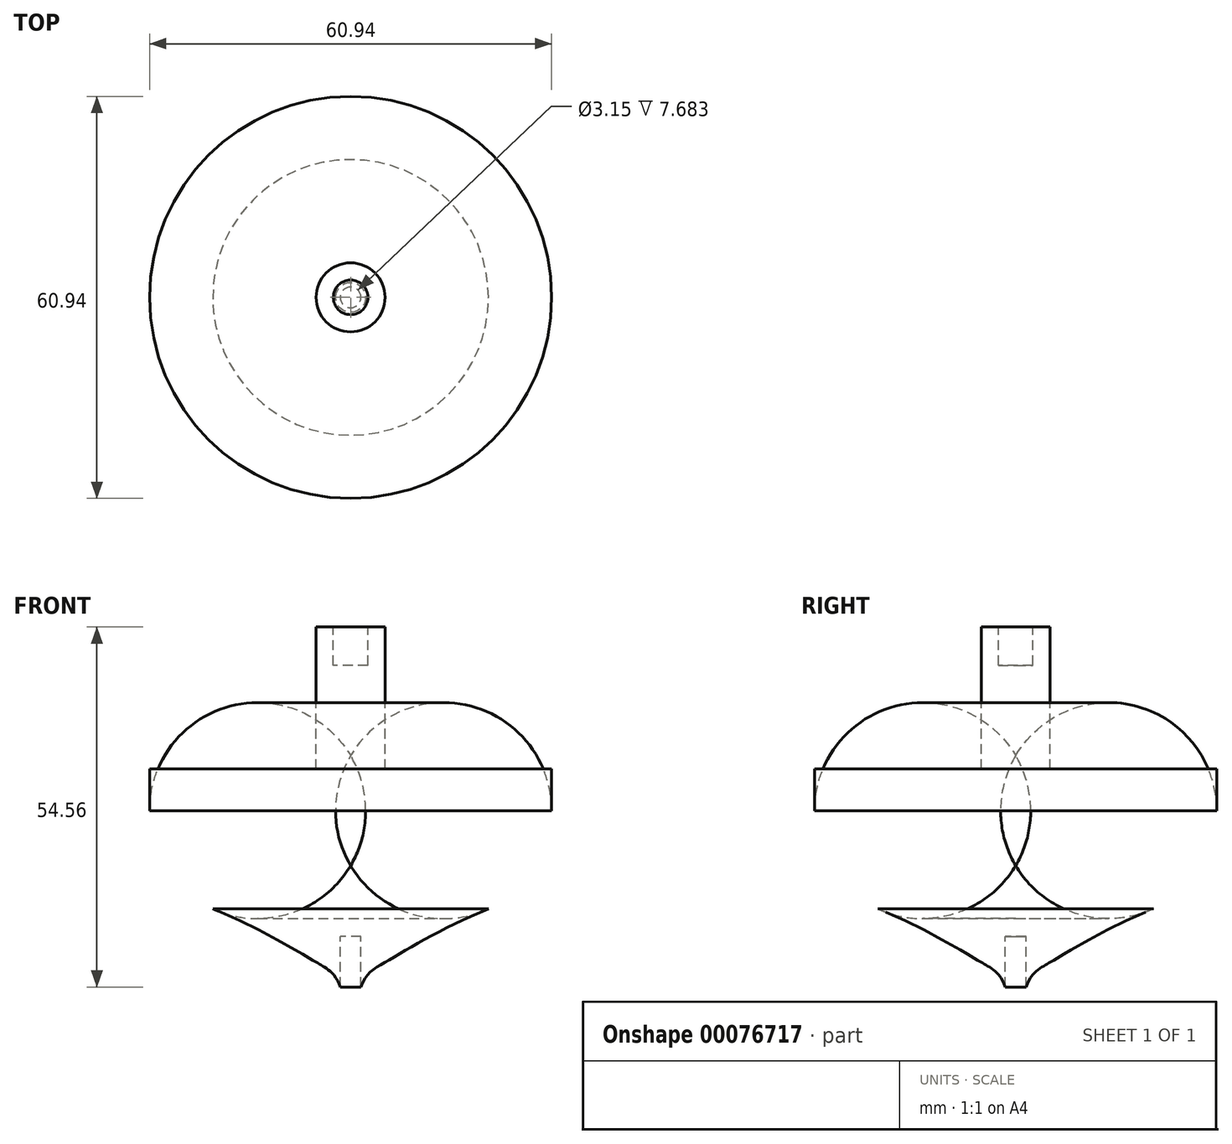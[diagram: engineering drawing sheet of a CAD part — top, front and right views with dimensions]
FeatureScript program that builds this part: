
annotation { "Feature Type Name" : "Feature", "Feature Type Description" : "" }
export const myFeature = defineFeature(function(context is Context, id is Id, definition is map)
    precondition{}
    {
        {
            var Q0;
            Q0=qCreatedBy(makeId("Front.planeOp"),FACE);
            var sketch = newSketch(context, id + "F0", { "sketchPlane" : qUnion([Q0])});
            skLineSegment(sketch, "E0", {"start": v(30.47, 32.63) * mm, "end": v(30.47, 38.92) * mm});
            skLineSegment(sketch, "E1", {"start": v(30.47, 38.92) * mm, "end": v(5.23, 38.92) * mm});
            skLineSegment(sketch, "E2", {"start": v(5.23, 38.92) * mm, "end": v(5.23, 60.45) * mm});
            skLineSegment(sketch, "E3", {"start": v(5.23, 60.45) * mm, "end": v(2.62, 60.45) * mm});
            skLineSegment(sketch, "E4", {"start": v(0, 54.65) * mm, "end": v(0, 13.57) * mm});
            skPoint(sketch, "E5.visualSharp", {"position": v(30.47, 21.88) * mm});
            skArc(sketch, "E5.filletArc", {"start": v(20.89, 17.73) * mm, "mid": v(27.86, 23.77) * mm, "end": v(30.47, 32.63) * mm});
            skFitSpline(sketch, "E6", {"points": [v(1.57, 5.89) * mm, v(5.27, 9.67) * mm, v(20.89, 17.73) * mm], "startDerivative": vector(5.88, 17.82) * mm, "endDerivative": vector(31.03, 12.31) * mm});
            skLineSegment(sketch, "E7", {"start": v(1.57, 5.89) * mm, "end": v(1.57, 13.57) * mm});
            skLineSegment(sketch, "E8", {"start": v(1.57, 13.57) * mm, "end": v(0, 13.57) * mm});
            skPoint(sketch, "E9.orphan", {"position": v(0, 10.59) * mm});
            skLineSegment(sketch, "E10", {"start": v(2.62, 60.45) * mm, "end": v(2.62, 54.65) * mm});
            skLineSegment(sketch, "E11", {"start": v(2.62, 54.65) * mm, "end": v(0, 54.65) * mm});
            skPoint(sketch, "E12.orphan", {"position": v(0, 60.45) * mm});
            skSolve(sketch);
        }
        {
            var Q0;
            Q0=makeQuery(id+"F0.imprint","IMPRINT",FACE,{"disambiguationData":[TD([[makeQuery(id+"F0.imprint","IMPRINT",EDGE,{"derivedFrom":sQuery(id+"F0.wireOp",EDGE,"E0")}),1.0]])]});
            var Q1;
            Q1=sQuery(id+"F0.wireOp",EDGE,"E4");
            revolve(context, id + "F1", {"entities" : qUnion([Q0]), "axis" : qUnion([Q1]), "revolveType" : RevolveType.FULL});
        }
    });
